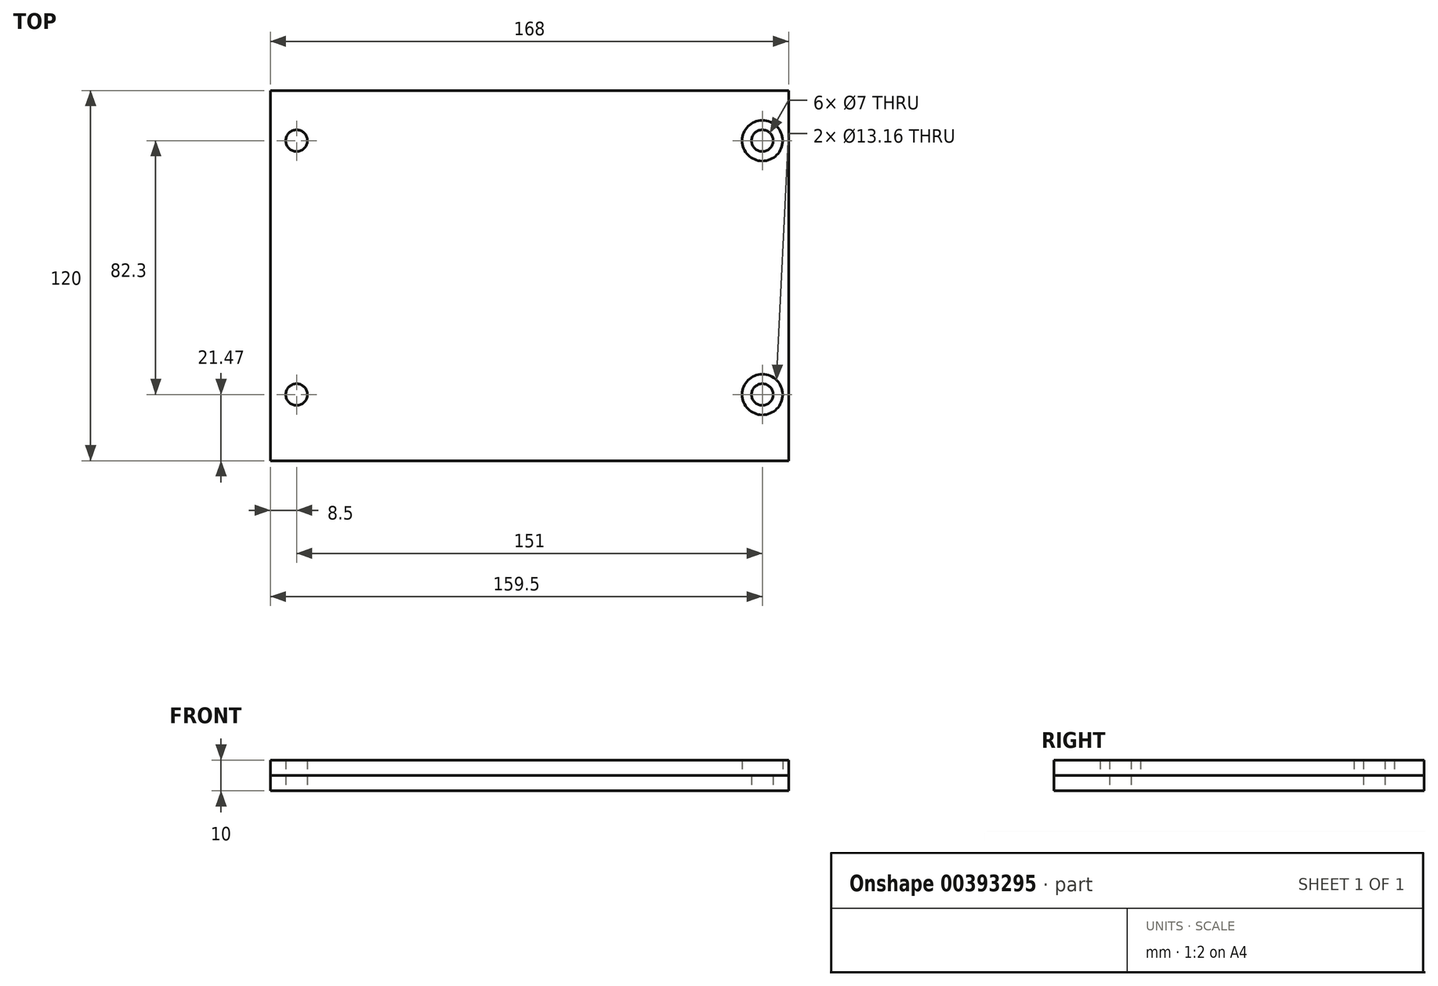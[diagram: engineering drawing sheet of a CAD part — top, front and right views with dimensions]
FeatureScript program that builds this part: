
annotation { "Feature Type Name" : "Feature", "Feature Type Description" : "" }
export const myFeature = defineFeature(function(context is Context, id is Id, definition is map)
    precondition{}
    {
        {
            var Q0;
            Q0=qCreatedBy(makeId("Top.planeOp"),FACE);
            var sketch = newSketch(context, id + "F0", { "sketchPlane" : qUnion([Q0])});
            skLineSegment(sketch, "E0.bottom", {"start": v(-84, 60) * mm, "end": v(84, 60) * mm});
            skLineSegment(sketch, "E0.top", {"start": v(-84, -60) * mm, "end": v(84, -60) * mm});
            skLineSegment(sketch, "E0.left", {"start": v(-84, 60) * mm, "end": v(-84, -60) * mm});
            skLineSegment(sketch, "E0.right", {"start": v(84, 60) * mm, "end": v(84, -60) * mm});
            skCircle(sketch, "E1", {"center": v(-75.5, 43.77) * mm, "radius": 3.5 * mm});
            skCircle(sketch, "E2", {"center": v(-75.5, -38.53) * mm, "radius": 3.5 * mm});
            skCircle(sketch, "E3.MirrorC", {"center": v(75.5, 43.77) * mm, "radius": 3.5 * mm});
            skCircle(sketch, "E4.MirrorC", {"center": v(75.5, -38.53) * mm, "radius": 3.5 * mm});
            skLineSegment(sketch, "E5", {"start": v(0, 60) * mm, "end": v(0, -60) * mm, "construction": true});
            skLineSegment(sketch, "E6", {"start": v(-84, 0) * mm, "end": v(84, 0) * mm, "construction": true});
            skPoint(sketch, "E7", {"position": v(0, 0) * mm});
            skSolve(sketch);
        }
        {
            var Q0;
            Q0=makeQuery(id+"F0.imprint","IMPRINT",FACE,{"disambiguationData":[TD([[makeQuery(id+"F0.imprint","IMPRINT",EDGE,{"derivedFrom":sQuery(id+"F0.wireOp",EDGE,"E0.bottom")}),-1.0]])]});
            extrude(context, id + "F1", {"entities" : qUnion([Q0]), "depth" : 5 * mm});
        }
        {
            var Q0;
            Q0=makeQuery(id+"F1.opExtrude","CAP_FACE",FACE,{"disambiguationData":[OSD([sQuery(id+"F0.wireOp",EDGE,"E0.bottom"),sQuery(id+"F0.wireOp",EDGE,"E0.top"),sQuery(id+"F0.wireOp",EDGE,"E0.left"),sQuery(id+"F0.wireOp",EDGE,"E0.right"),sQuery(id+"F0.wireOp",EDGE,"E1"),sQuery(id+"F0.wireOp",EDGE,"E2"),sQuery(id+"F0.wireOp",EDGE,"E3.MirrorC"),sQuery(id+"F0.wireOp",EDGE,"E4.MirrorC")])],"isStart":false});
            var sketch = newSketch(context, id + "F2", { "sketchPlane" : qUnion([Q0])});
            skCircle(sketch, "E8", {"center": v(-75.5, -38.53) * mm, "radius": 6.58 * mm});
            skCircle(sketch, "E9.MirrorC", {"center": v(75.5, -38.53) * mm, "radius": 6.58 * mm});
            skCircle(sketch, "E10", {"center": v(-75.5, 43.77) * mm, "radius": 6.58 * mm});
            skCircle(sketch, "E11.MirrorC", {"center": v(75.5, 43.77) * mm, "radius": 6.58 * mm});
            skSolve(sketch);
        }
        {
            var Q0;
            Q0=makeQuery(id+"F2.imprint","IMPRINT",FACE,{"disambiguationData":[TD([[makeQuery(id+"F2.imprint","IMPRINT",EDGE,{"derivedFrom":sQuery(id+"F2.wireOp",EDGE,"E8")}),1.0]])]});
            var Q1;
            Q1=makeQuery(id+"F2.imprint","IMPRINT",FACE,{"disambiguationData":[TD([[makeQuery(id+"F2.imprint","IMPRINT",EDGE,{"derivedFrom":sQuery(id+"F2.wireOp",EDGE,"E10")}),1.0]])]});
            var Q2;
            Q2=makeQuery(id+"F2.imprint","IMPRINT",FACE,{"disambiguationData":[TD([[makeQuery(id+"F2.imprint","IMPRINT",EDGE,{"derivedFrom":sQuery(id+"F2.wireOp",EDGE,"E11.MirrorC")}),-1.0]])]});
            var Q3;
            Q3=makeQuery(id+"F2.imprint","IMPRINT",FACE,{"disambiguationData":[TD([[makeQuery(id+"F2.imprint","IMPRINT",EDGE,{"derivedFrom":sQuery(id+"F2.wireOp",EDGE,"E9.MirrorC")}),-1.0]])]});
            var Q4;
            Q4=sQuery(id+"F2.wireOp",EDGE,"E8");
            extrude(context, id + "F3", {"entities" : qUnion([Q0, Q1, Q2, Q3]), "surfaceEntities" : qUnion([Q4]), "depth" : 5 * mm});
        }
    });
